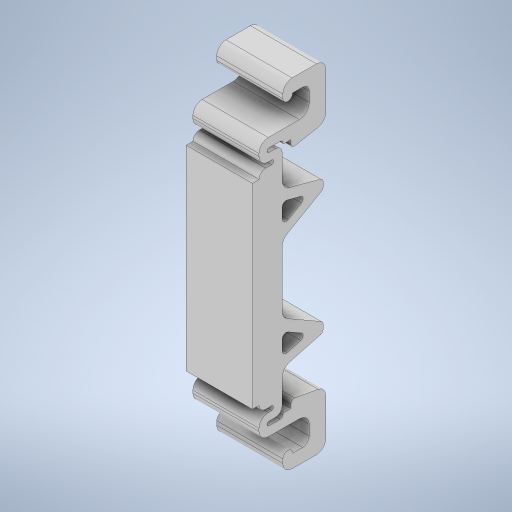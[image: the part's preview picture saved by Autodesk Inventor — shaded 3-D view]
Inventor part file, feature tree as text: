
AUTODESK INVENTOR PART (.ipt)
format: ipt  version: 2023 (Build 270158030, 158C)  size: 629,248 bytes
history: native  units: mm
features: other x4, extrude x2, mirror x1, sketch x1, projected_geometry x1
ambient origin geometry x8: Origin, YZ Plane, XZ Plane, XY Plane, X Axis, Y Axis, Z Axis, Center Point
bodies: Body1 (feature_tree), Body2 (feature_tree)
feature tree (9):
  other  "DIN-rail"
  other  "Blocks"
  extrude  "Extrusion5"  Depth=1.0mm
  extrude  "Extrusion6"  Depth=35.0mm
  mirror  "Mirror2"
  other  "DIN-rail-clip-generic-V1.0"
  sketch  "Sketch6"  dims[d0=1.0mm d1=1.0mm d5=35.0mm d8=7.3mm d9=1.0mm d10=1.0mm d11=2.0mm d12=2.0mm d13=12.7mm d15=12.7mm d16=4.8mm d17=4.8mm d20=1.0mm d21=1.0mm d22=2.0mm d63=3.0mm d68=23.446722mm d71=0.937247mm d73=0.268963mm d74=0.352771mm d79=1.536323mm d85=0.790525mm d87=1.178422mm d88=0.790667mm d89=1.583516mm d90=5.132142mm d92=2.277882mm d93=2.745808mm d95=1.718388mm d96=0.72523mm d97=3.434383mm d99=1.223642mm d100=0.420939mm d101=1.2mm d102=0.8mm d103=1.8mm d104=0.8mm d105=2.6mm d106=0.10359mm d107=2.0mm d108=0.2mm d109=1.0mm d110=0.9mm d111=0.453644mm d112=1.2mm d113=1.4mm d114=0.037497mm d115=0.017085mm d116=0.527749mm d117=0.098913mm d118=0.689958mm d119=0.668213mm d120=0.705542mm d121=0.541172mm d122=1.737399mm d123=0.201916mm d124=0.5mm d125=0.302867mm d126=1.178422mm d127=3.970876mm d128=0.664321mm d129=1.031647mm d130=0.660389mm d131=0.064915mm d132=1.807627mm d133=1.565015mm d134=0.929795mm d136=0.743817mm d138=0.348214mm d139=0.310128mm d140=0.916882mm d141=2.209313mm d142=0.166244mm d143=0.176385mm d144=0.33806mm d145=0.652404mm d147=0.433822mm d148=1.6mm d149=0.56mm d150=1.034228mm d151=3.0mm d152=1.4mm d153=0.514445mm d154=0.593437mm d155=6.438638mm d156=0.946159mm d157=0.175634mm d158=0.264169mm d159=1.4mm d160=1.0mm d162=2.1mm d163=2.3mm d179=10.0mm d180=0.0mm d259=2.5mm d268=6.0mm d269=2.0mm d270=4.0mm d279=3.0mm d283=1.5mm d290=1.5mm d291=0.75mm d293=1.0mm d295=1.0mm d296=10.0mm d297=0.0mm d298=75.0deg d299=60.0deg d300=0.2mm d301=1.4mm d303=1.5mm d304=1.5mm d305=1.5mm d306=1.5mm d307=0.5mm d310=0.4mm d320=0.2mm d322=0.1mm d333=0.1mm d334=0.4mm d338=1.6mm d339=3.0mm d340=0.6mm d341=0.6mm d342=1.2mm d343=1.4mm d344=1.4mm d345=1.4mm d346=0.3mm d348=3.5mm d349=2.0mm d350=1.0mm d351=0.3mm d354=0.2mm d355=0.6mm d356=1.2mm d357=0.5mm d358=1.4mm d359=1.4mm d360=0.6mm d361=1.5mm]
  other  "DIN-clip"
  projected_geometry  "Projected Loop3"
